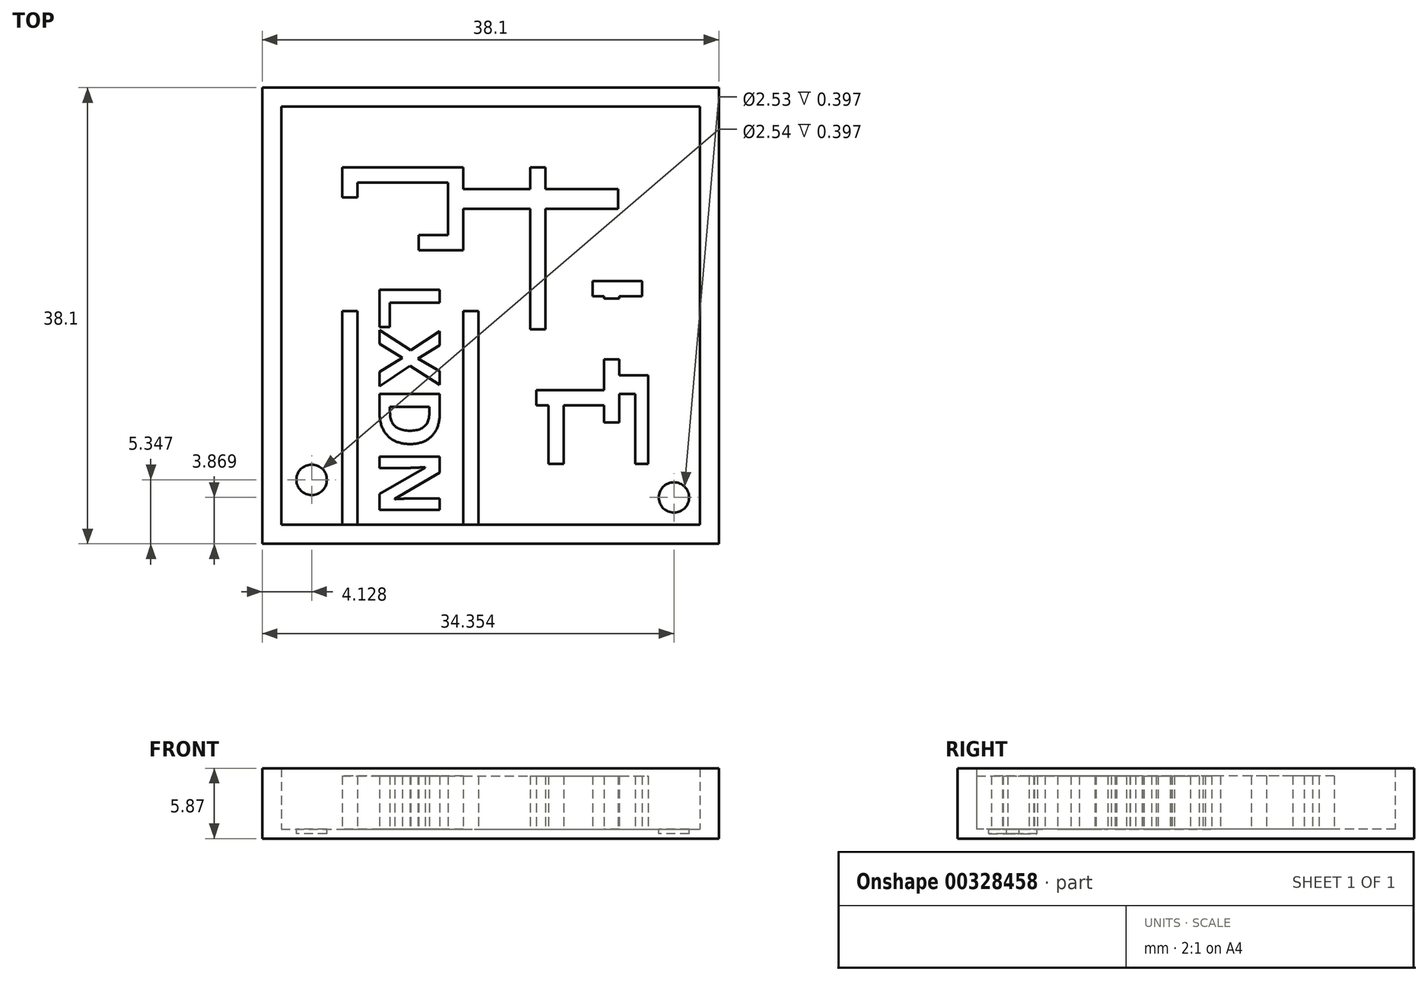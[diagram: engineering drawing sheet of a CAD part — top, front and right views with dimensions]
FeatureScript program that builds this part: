
annotation { "Feature Type Name" : "Feature", "Feature Type Description" : "" }
export const myFeature = defineFeature(function(context is Context, id is Id, definition is map)
    precondition{}
    {
        {
            var Q0;
            Q0=qCreatedBy(makeId("Top.planeOp"),FACE);
            var sketch = newSketch(context, id + "F0", { "sketchPlane" : qUnion([Q0])});
            skLineSegment(sketch, "E0.bottom", {"start": v(-23.48, 13.85) * mm, "end": v(14.62, 13.85) * mm});
            skLineSegment(sketch, "E0.top", {"start": v(-23.48, -24.25) * mm, "end": v(14.62, -24.25) * mm});
            skLineSegment(sketch, "E0.left", {"start": v(-23.48, 13.85) * mm, "end": v(-23.48, -24.25) * mm});
            skLineSegment(sketch, "E0.right", {"start": v(14.62, 13.85) * mm, "end": v(14.62, -24.25) * mm});
            skSolve(sketch);
        }
        {
            var Q0;
            Q0=makeQuery(id+"F0.imprint","IMPRINT",FACE,{"disambiguationData":[TD([[makeQuery(id+"F0.imprint","IMPRINT",EDGE,{"derivedFrom":sQuery(id+"F0.wireOp",EDGE,"E0.bottom")}),-1.0]])]});
            extrude(context, id + "F1", {"entities" : qUnion([Q0]), "depth" : 0.8 * mm});
        }
        {
            var Q0;
            Q0=makeQuery(id+"F1.opExtrude","CAP_FACE",FACE,{"disambiguationData":[OSD([sQuery(id+"F0.wireOp",EDGE,"E0.bottom"),sQuery(id+"F0.wireOp",EDGE,"E0.top"),sQuery(id+"F0.wireOp",EDGE,"E0.left"),sQuery(id+"F0.wireOp",EDGE,"E0.right")])],"isStart":false});
            var sketch = newSketch(context, id + "F2", { "sketchPlane" : qUnion([Q0])});
            skLineSegment(sketch, "E1.0", {"start": v(-21.9, 12.26) * mm, "end": v(13.03, 12.26) * mm});
            skLineSegment(sketch, "E1.1", {"start": v(-21.9, 12.26) * mm, "end": v(-21.9, -22.67) * mm});
            skLineSegment(sketch, "E1.2", {"start": v(-21.9, -22.67) * mm, "end": v(13.03, -22.67) * mm});
            skLineSegment(sketch, "E1.3", {"start": v(13.03, 12.26) * mm, "end": v(13.03, -22.67) * mm});
            skSolve(sketch);
        }
        {
            var Q0;
            Q0=makeQuery(id+"F2.imprint","IMPRINT",FACE,{"disambiguationData":[TD([[makeQuery(id+"F2.imprint","IMPRINT",EDGE,{"derivedFrom":sQuery(id+"F2.wireOp",EDGE,"E1.0")}),1.0]])]});
            extrude(context, id + "F3", {"entities" : qUnion([Q0]), "operationType" : NewBodyOperationType.ADD, "depth" : 5.08 * mm});
        }
        {
            var Q0;
            Q0=makeQuery(id+"F1.opExtrude","CAP_FACE",FACE,{"disambiguationData":[OSD([sQuery(id+"F0.wireOp",EDGE,"E0.bottom"),sQuery(id+"F0.wireOp",EDGE,"E0.top"),sQuery(id+"F0.wireOp",EDGE,"E0.left"),sQuery(id+"F0.wireOp",EDGE,"E0.right")])],"isStart":false});
            var sketch = newSketch(context, id + "F4", { "sketchPlane" : qUnion([Q0])});
            skLineSegment(sketch, "E2.bottom", {"start": v(-16.81, -22.67) * mm, "end": v(-15.54, -22.67) * mm});
            skLineSegment(sketch, "E2.left", {"start": v(-16.81, -22.67) * mm, "end": v(-16.81, -4.82) * mm});
            skLineSegment(sketch, "E2.right", {"start": v(-15.54, -22.67) * mm, "end": v(-15.54, -4.82) * mm});
            skLineSegment(sketch, "E3", {"start": v(-15.54, -4.82) * mm, "end": v(-16.81, -4.82) * mm});
            skLineSegment(sketch, "E4.top", {"start": v(-15.54, 5.9) * mm, "end": v(-7.96, 5.9) * mm});
            skLineSegment(sketch, "E5.left", {"start": v(-7.96, 5.9) * mm, "end": v(-7.96, 1.53) * mm});
            skLineSegment(sketch, "E5.right", {"start": v(-6.7, 7.18) * mm, "end": v(-6.7, 5.37) * mm});
            skLineSegment(sketch, "E6.right", {"start": v(-10.43, 1.53) * mm, "end": v(-10.43, 0.26) * mm});
            skLineSegment(sketch, "E7.top", {"start": v(-6.7, -4.82) * mm, "end": v(-5.42, -4.82) * mm});
            skLineSegment(sketch, "E8", {"start": v(-10.43, 0.26) * mm, "end": v(-6.7, 0.26) * mm});
            skLineSegment(sketch, "E9", {"start": v(-5.42, -4.82) * mm, "end": v(-5.42, -22.67) * mm});
            skLineSegment(sketch, "E10", {"start": v(-6.7, -22.67) * mm, "end": v(-5.42, -22.67) * mm});
            skLineSegment(sketch, "E11", {"start": v(-6.7, -22.67) * mm, "end": v(-6.7, -4.82) * mm});
            skLineSegment(sketch, "E12.bottom", {"start": v(-1.1, 7.18) * mm, "end": v(0.17, 7.18) * mm});
            skLineSegment(sketch, "E12.top", {"start": v(-1.1, -6.35) * mm, "end": v(0.17, -6.35) * mm});
            skLineSegment(sketch, "E12.left", {"start": v(-1.1, 7.18) * mm, "end": v(-1.1, 5.37) * mm});
            skLineSegment(sketch, "E12.right", {"start": v(0.17, 7.18) * mm, "end": v(0.17, 5.37) * mm});
            skPoint(sketch, "E13.oppositeSnap0", {"position": v(-6.7, 3.72) * mm});
            skLineSegment(sketch, "E13.bottom", {"start": v(-6.7, 5.37) * mm, "end": v(-1.1, 5.37) * mm});
            skLineSegment(sketch, "E13.top", {"start": v(-6.7, 3.72) * mm, "end": v(-1.1, 3.72) * mm});
            skLineSegment(sketch, "E13.right", {"start": v(6.21, 5.37) * mm, "end": v(6.21, 3.72) * mm});
            skLineSegment(sketch, "E14.top", {"start": v(5.05, -14.12) * mm, "end": v(6.32, -14.12) * mm});
            skLineSegment(sketch, "E15.bottom", {"start": v(4.1, -2.32) * mm, "end": v(8.2, -2.32) * mm});
            skLineSegment(sketch, "E15.top", {"start": v(4.1, -3.59) * mm, "end": v(5.05, -3.59) * mm});
            skLineSegment(sketch, "E15.left", {"start": v(4.1, -2.32) * mm, "end": v(4.1, -3.59) * mm});
            skLineSegment(sketch, "E15.right", {"start": v(8.2, -2.32) * mm, "end": v(8.2, -3.59) * mm});
            skLineSegment(sketch, "E16.trimOffspring", {"start": v(6.32, -3.59) * mm, "end": v(6.32, -3.77) * mm});
            skLineSegment(sketch, "E17.trimOffspring", {"start": v(5.05, -3.59) * mm, "end": v(5.05, -3.77) * mm});
            skLineSegment(sketch, "E18.trimOffspring", {"start": v(6.32, -3.59) * mm, "end": v(8.2, -3.59) * mm});
            skLineSegment(sketch, "E19.trimOffspring", {"start": v(0.17, 3.72) * mm, "end": v(0.17, -6.35) * mm});
            skLineSegment(sketch, "E20.trimOffspring", {"start": v(-1.1, 3.72) * mm, "end": v(-1.1, -6.35) * mm});
            skLineSegment(sketch, "E21.trimOffspring", {"start": v(0.17, 3.72) * mm, "end": v(6.21, 3.72) * mm});
            skLineSegment(sketch, "E22.trimOffspring", {"start": v(0.17, 5.37) * mm, "end": v(6.21, 5.37) * mm});
            skLineSegment(sketch, "E23.trimOffspring", {"start": v(-6.7, 3.72) * mm, "end": v(-6.7, 0.26) * mm});
            skLineSegment(sketch, "E24.bottom", {"start": v(-0.6, -11.43) * mm, "end": v(5.05, -11.43) * mm});
            skLineSegment(sketch, "E24.top", {"start": v(-0.6, -12.7) * mm, "end": v(0.4, -12.7) * mm});
            skLineSegment(sketch, "E24.left", {"start": v(-0.6, -11.43) * mm, "end": v(-0.6, -12.7) * mm});
            skLineSegment(sketch, "E25.top", {"start": v(7.66, -17.59) * mm, "end": v(8.71, -17.59) * mm});
            skLineSegment(sketch, "E25.left", {"start": v(7.66, -11.73) * mm, "end": v(7.66, -17.59) * mm});
            skLineSegment(sketch, "E25.right", {"start": v(8.71, -10.17) * mm, "end": v(8.71, -17.59) * mm});
            skLineSegment(sketch, "E26.trimOffspring", {"start": v(5.05, -8.85) * mm, "end": v(5.05, -11.43) * mm});
            skLineSegment(sketch, "E27.trimOffspring", {"start": v(6.32, -8.85) * mm, "end": v(6.32, -10.17) * mm});
            skLineSegment(sketch, "E28", {"start": v(5.05, -8.85) * mm, "end": v(6.32, -8.85) * mm});
            skLineSegment(sketch, "E29", {"start": v(6.32, -3.77) * mm, "end": v(5.05, -3.77) * mm});
            skLineSegment(sketch, "E30.trimOffspring", {"start": v(5.05, -12.7) * mm, "end": v(5.05, -14.12) * mm});
            skLineSegment(sketch, "E31.top", {"start": v(-16.81, 4.68) * mm, "end": v(-15.54, 4.68) * mm});
            skLineSegment(sketch, "E32", {"start": v(-10.43, 1.53) * mm, "end": v(-7.96, 1.53) * mm});
            skLineSegment(sketch, "E33.trimOffspring", {"start": v(1.67, -12.7) * mm, "end": v(5.05, -12.7) * mm});
            skLineSegment(sketch, "E34.top", {"start": v(0.4, -17.59) * mm, "end": v(1.67, -17.59) * mm});
            skLineSegment(sketch, "E34.left", {"start": v(0.4, -12.7) * mm, "end": v(0.4, -17.59) * mm});
            skLineSegment(sketch, "E34.right", {"start": v(1.67, -12.66) * mm, "end": v(1.67, -17.59) * mm});
            skLineSegment(sketch, "E35", {"start": v(6.32, -14.12) * mm, "end": v(6.32, -11.73) * mm});
            skLineSegment(sketch, "E36", {"start": v(6.32, -10.17) * mm, "end": v(8.71, -10.17) * mm});
            skLineSegment(sketch, "E37", {"start": v(-6.7, 7.18) * mm, "end": v(-16.81, 7.18) * mm});
            skLineSegment(sketch, "E38", {"start": v(-16.81, 7.18) * mm, "end": v(-16.81, 4.68) * mm});
            skLineSegment(sketch, "E39", {"start": v(-15.54, 5.9) * mm, "end": v(-15.54, 4.68) * mm});
            skLineSegment(sketch, "E40", {"start": v(-21.9, -22.67) * mm, "end": v(-16.81, -22.67) * mm});
            skCircle(sketch, "E41", {"center": v(-19.35, -18.9) * mm, "radius": 1.27 * mm});
            skPoint(sketch, "E41.centerSnap0", {"position": v(-19.35, -22.67) * mm});
            skLineSegment(sketch, "E42", {"start": v(13.03, -22.67) * mm, "end": v(8.71, -22.67) * mm});
            skCircle(sketch, "E43", {"center": v(10.87, -20.38) * mm, "radius": 1.27 * mm});
            skPoint(sketch, "E43.centerSnap0", {"position": v(10.87, -22.67) * mm});
            skLineSegment(sketch, "E44", {"start": v(6.32, -11.73) * mm, "end": v(7.66, -11.73) * mm});
            skSolve(sketch);
        }
        {
            var Q0;
            Q0=makeQuery(id+"F4.imprint","IMPRINT",FACE,{"disambiguationData":[TD([[makeQuery(id+"F4.imprint","IMPRINT",EDGE,{"derivedFrom":sQuery(id+"F4.wireOp",EDGE,"E2.top")}),-1.0]])]});
            var Q1;
            Q1=makeQuery(id+"F4.imprint","IMPRINT",FACE,{"disambiguationData":[TD([[makeQuery(id+"F4.imprint","IMPRINT",EDGE,{"derivedFrom":sQuery(id+"F4.wireOp",EDGE,"E2.bottom")}),1.0]])]});
            var Q2;
            Q2=makeQuery(id+"F4.imprint","IMPRINT",FACE,{"disambiguationData":[TD([[makeQuery(id+"F4.imprint","IMPRINT",EDGE,{"derivedFrom":sQuery(id+"F4.wireOp",EDGE,"V4mLeiWr-R0nf-PX4E-hSja-4r4zASFe8L39.top")}),-1.0]])]});
            var Q3;
            Q3=makeQuery(id+"F4.imprint","IMPRINT",FACE,{"disambiguationData":[TD([[makeQuery(id+"F4.imprint","IMPRINT",EDGE,{"derivedFrom":sQuery(id+"F4.wireOp",EDGE,"E7.top")}),-1.0]])]});
            var Q4;
            Q4=makeQuery(id+"F4.imprint","IMPRINT",FACE,{"disambiguationData":[TD([[makeQuery(id+"F4.imprint","IMPRINT",EDGE,{"derivedFrom":sQuery(id+"F4.wireOp",EDGE,"E14.top")}),1.0]])]});
            var Q5;
            Q5=makeQuery(id+"F4.imprint","IMPRINT",FACE,{"disambiguationData":[TD([[makeQuery(id+"F4.imprint","IMPRINT",EDGE,{"derivedFrom":sQuery(id+"F4.wireOp",EDGE,"E15.bottom")}),-1.0]])]});
            var Q6;
            Q6=makeQuery(id+"F4.imprint","IMPRINT",FACE,{"disambiguationData":[TD([[makeQuery(id+"F4.imprint","IMPRINT",EDGE,{"derivedFrom":sQuery(id+"F4.wireOp",EDGE,"E4.top")}),1.0]])]});
            extrude(context, id + "F5", {"entities" : qUnion([Q0, Q1, Q2, Q3, Q4, Q5, Q6]), "operationType" : NewBodyOperationType.ADD, "depth" : 4.44 * mm});
        }
        {
            var Q0;
            Q0=makeQuery(id+"F1.opExtrude","CAP_FACE",FACE,{"disambiguationData":[OSD([sQuery(id+"F0.wireOp",EDGE,"E0.bottom"),sQuery(id+"F0.wireOp",EDGE,"E0.top"),sQuery(id+"F0.wireOp",EDGE,"E0.left"),sQuery(id+"F0.wireOp",EDGE,"E0.right")])],"isStart":false});
            var sketch = newSketch(context, id + "F6", { "sketchPlane" : qUnion([Q0])});
            skText(sketch, "E45", { "text": "LXDN\n", "fontName": "OpenSans-Bold.ttf"});
            const initialGuessF6  = {"E45": [-0.0137, -0.00241, 0, -1, 0.00508]};
            skSetInitialGuess(sketch, initialGuessF6);
            skSolve(sketch);
        }
        {
            var Q0;
            Q0 = qSketchRegion(id + "F6", true);
            extrude(context, id + "F7", {"entities" : qUnion([Q0]), "operationType" : NewBodyOperationType.ADD, "depth" : 4.44 * mm});
        }
        {
            var Q0;
            Q0=makeQuery(id+"F4.imprint","IMPRINT",FACE,{"disambiguationData":[TD([[makeQuery(id+"F4.imprint","IMPRINT",EDGE,{"derivedFrom":sQuery(id+"F4.wireOp",EDGE,"E41")}),1.0]])]});
            var Q1;
            Q1=makeQuery(id+"F4.imprint","IMPRINT",FACE,{"disambiguationData":[TD([[makeQuery(id+"F4.imprint","IMPRINT",EDGE,{"derivedFrom":sQuery(id+"F4.wireOp",EDGE,"E43")}),1.0]])]});
            extrude(context, id + "F8", {"entities" : qUnion([Q0, Q1]), "operationType" : NewBodyOperationType.REMOVE, "oppositeDirection" : true, "depth" : 0.4 * mm});
        }
    });
